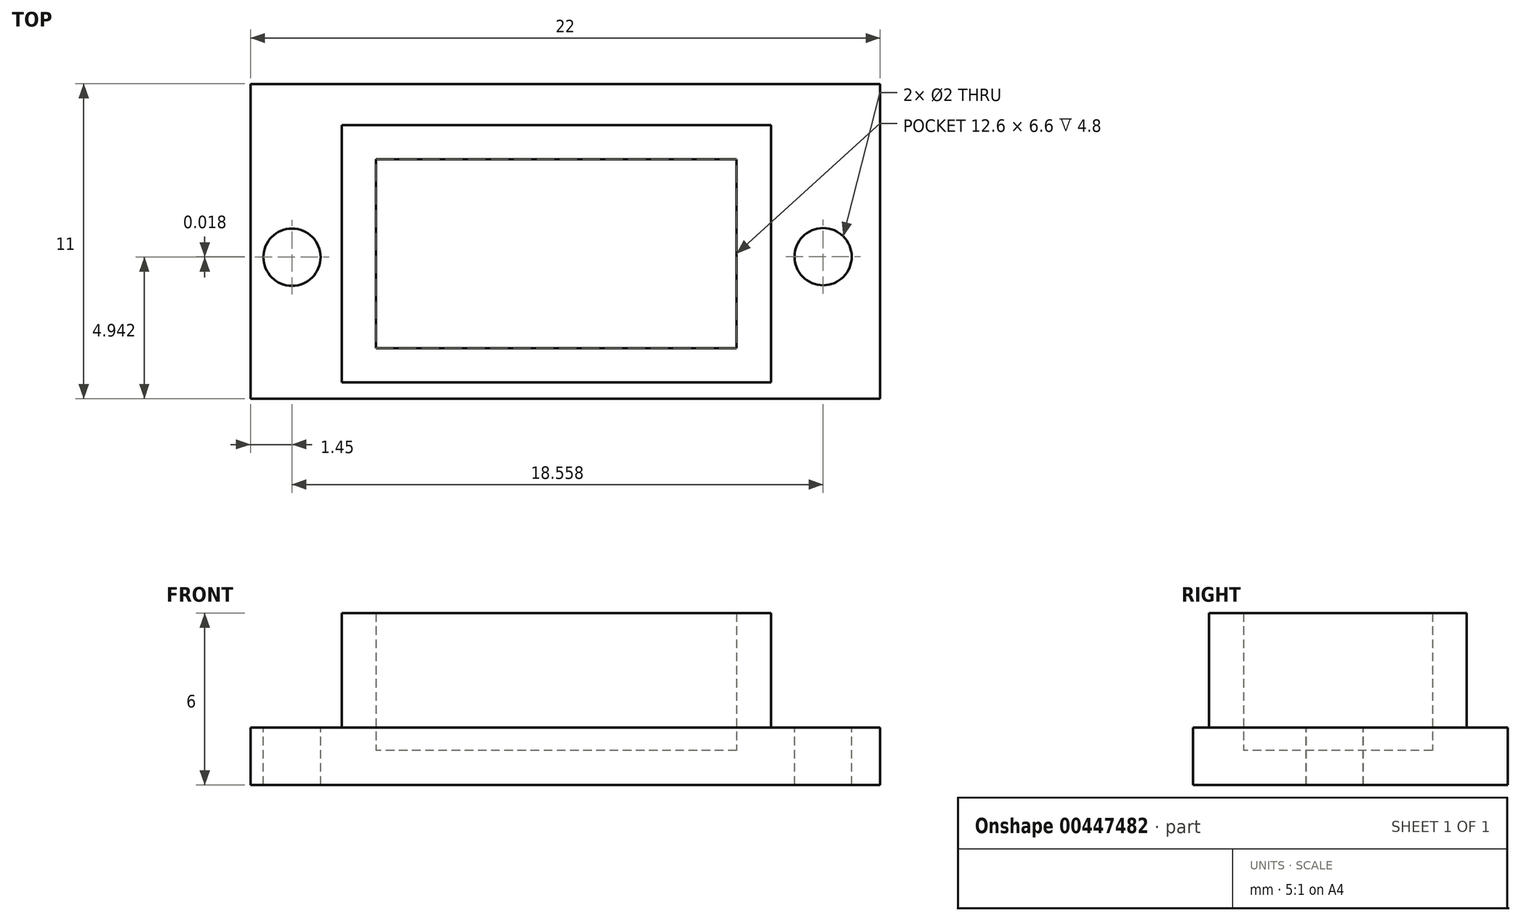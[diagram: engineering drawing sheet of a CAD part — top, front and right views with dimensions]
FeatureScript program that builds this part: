
annotation { "Feature Type Name" : "Feature", "Feature Type Description" : "" }
export const myFeature = defineFeature(function(context is Context, id is Id, definition is map)
    precondition{}
    {
        {
            var Q0;
            Q0=qCreatedBy(makeId("Top.planeOp"),FACE);
            var sketch = newSketch(context, id + "F0", { "sketchPlane" : qUnion([Q0])});
            skLineSegment(sketch, "E0.bottom", {"start": v(-0.42, 6.04) * mm, "end": v(21.58, 6.04) * mm});
            skLineSegment(sketch, "E0.top", {"start": v(-0.42, -4.96) * mm, "end": v(21.58, -4.96) * mm});
            skLineSegment(sketch, "E0.left", {"start": v(-0.42, 6.04) * mm, "end": v(-0.42, -4.96) * mm});
            skLineSegment(sketch, "E0.right", {"start": v(21.58, 6.04) * mm, "end": v(21.58, -4.96) * mm});
            skSolve(sketch);
        }
        {
            var Q0;
            Q0=makeQuery(id+"F0.imprint","IMPRINT",FACE,{"disambiguationData":[TD([[makeQuery(id+"F0.imprint","IMPRINT",EDGE,{"derivedFrom":sQuery(id+"F0.wireOp",EDGE,"E0.bottom")}),-1.0]])]});
            extrude(context, id + "F1", {"entities" : qUnion([Q0]), "depth" : 2 * mm, "offsetDistance" : 25 * mm});
        }
        {
            var Q0;
            Q0=qCreatedBy(makeId("Top.planeOp"),FACE);
            var sketch = newSketch(context, id + "F2", { "sketchPlane" : qUnion([Q0])});
            skLineSegment(sketch, "E1.bottom", {"start": v(2.77, -4.4) * mm, "end": v(17.77, -4.4) * mm});
            skLineSegment(sketch, "E1.top", {"start": v(2.77, 4.6) * mm, "end": v(17.77, 4.6) * mm});
            skLineSegment(sketch, "E1.left", {"start": v(2.77, -4.4) * mm, "end": v(2.77, 4.6) * mm});
            skLineSegment(sketch, "E1.right", {"start": v(17.77, -4.4) * mm, "end": v(17.77, 4.6) * mm});
            skSolve(sketch);
        }
        {
            var Q0;
            Q0 = qSketchRegion(id + "F2", true);
            extrude(context, id + "F3", {"entities" : qUnion([Q0]), "operationType" : NewBodyOperationType.ADD, "depth" : 6 * mm, "offsetDistance" : 25 * mm});
        }
        {
            var Q0;
            Q0=makeQuery(id+"F3.opExtrude","CAP_FACE",FACE,{"disambiguationData":[OSD([sQuery(id+"F2.wireOp",EDGE,"E1.bottom"),sQuery(id+"F2.wireOp",EDGE,"E1.top"),sQuery(id+"F2.wireOp",EDGE,"E1.left"),sQuery(id+"F2.wireOp",EDGE,"E1.right")])],"isStart":false});
            shell(context, id + "F4", {"entities" : qUnion([Q0]), "thickness" : 1.2 * mm});
        }
        {
            var Q0;
            Q0=makeQuery(id+"F1.opExtrude","CAP_FACE",FACE,{"disambiguationData":[OSD([sQuery(id+"F0.wireOp",EDGE,"E0.bottom"),sQuery(id+"F0.wireOp",EDGE,"E0.top"),sQuery(id+"F0.wireOp",EDGE,"E0.left"),sQuery(id+"F0.wireOp",EDGE,"E0.right")])],"isStart":false});
            var sketch = newSketch(context, id + "F5", { "sketchPlane" : qUnion([Q0])});
            skCircle(sketch, "E2", {"center": v(1.03, -0.02) * mm, "radius": 1 * mm});
            skSolve(sketch);
        }
        {
            var Q0;
            {var subQ0=makeQuery(id+"F1.opExtrude","CAP_FACE",FACE,{"disambiguationData":[OSD([sQuery(id+"F0.wireOp",EDGE,"E0.bottom"),sQuery(id+"F0.wireOp",EDGE,"E0.top"),sQuery(id+"F0.wireOp",EDGE,"E0.left"),sQuery(id+"F0.wireOp",EDGE,"E0.right")])],"isStart":false});Q0=makeQuery(id+"F5.imprint","IMPRINT",FACE,{"disambiguationData":[TD([[makeQuery(id+"F5.imprint","IMPRINT",EDGE,{"derivedFrom":makeQuery(id+"F3.boolean.opBoolean","INTERSECT",EDGE,{"derivedFrom":[subQ0,makeQuery(id+"F3.opExtrude","SWEPT_FACE",FACE,{"disambiguationData":[OSD([sQuery(id+"F2.wireOp",EDGE,"E1.bottom")])]})]})}),-1.0]])]});}
            var sketch = newSketch(context, id + "F6", { "sketchPlane" : qUnion([Q0])});
            skCircle(sketch, "E3", {"center": v(19.59, 0) * mm, "radius": 1 * mm});
            skSolve(sketch);
        }
        {
            var Q0;
            Q0 = qSketchRegion(id + "F6", true);
            extrude(context, id + "F7", {"entities" : qUnion([Q0]), "operationType" : NewBodyOperationType.REMOVE, "oppositeDirection" : true, "depth" : 25 * mm, "offsetDistance" : 25 * mm});
        }
        {
            var Q0;
            Q0 = qSketchRegion(id + "F5", true);
            extrude(context, id + "F8", {"entities" : qUnion([Q0]), "operationType" : NewBodyOperationType.REMOVE, "oppositeDirection" : true, "depth" : 25 * mm, "offsetDistance" : 25 * mm});
        }
    });
